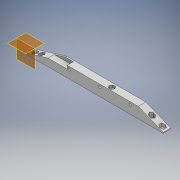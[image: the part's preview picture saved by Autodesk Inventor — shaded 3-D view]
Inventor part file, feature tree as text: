
AUTODESK INVENTOR PART (.ipt)
format: ipt  version: 2019 (Build 230136000, 136)  size: 250,368 bytes
history: native  units: mm
features: extrude x11, sketch x10, plane x7
ambient origin geometry x8: Origin, YZ Plane, XZ Plane, XY Plane, X Axis, Y Axis, Z Axis, Center Point
bodies: Solid1 (feature_tree)
feature tree (28):
  sketch  "Sketch1"  dims[d1=9.0mm d2=90.0deg]
  plane  "Work Plane2"
  sketch  "Sketch2"  dims[d6=3.2mm d7=3.2mm]
  plane  "Work Plane1"
  extrude  "klocek"  TaperAngle=90.0deg  [1 undecoded]
  plane  "Work Plane3"
  extrude  "prowadzenie osi"  Depth=3.2mm
  plane  "Work Plane4"
  sketch  "Sketch7"  dims[d15=3.2mm d17=3.2mm]
  sketch  "Sketch8"  dims[d18=36.5mm d26=3.2mm]
  extrude  "przedni skos"  Depth=3.2mm
  extrude  "tylni skos"  Depth=3.2mm
  plane  "Work Plane7"
  sketch  "Sketch5"  dims[d9=60.5mm d13=3.2mm]
  extrude  "hex insert middle"  Depth=3.2mm
  plane  "Work Plane6"
  sketch  "Sketch9"  dims[d27=48.0mm d28=3.2mm]
  extrude  "hex insert rear 1"  Depth=3.2mm
  plane  "Work Plane5"
  extrude  "hex insert rear 2"  Depth=5.0mm
  extrude  "hex insert front 1"  TaperAngle=0.0deg  [1 undecoded]
  extrude  "hex insert front 2"  Depth=8.0mm
  extrude  "ciecie przod"  Depth=5.9mm
  extrude  "sensor linii"  Depth=5.9mm
  sketch  "Sketch10"  dims[d32=15.0mm d33=5.0mm]
  sketch  "Sketch16"  dims[d38=11.0mm d39=0.0mm]
  sketch  "Sketch17"  dims[d61=3.2mm d62=8.0mm]
  sketch  "Sketch18"  dims[d63=12.5mm d64=52.0mm d65=36.5mm d67=13.0mm d68=0.0mm d70=7.5mm d71=0.0mm d77=5.0mm d78=0.0mm d80=12.0mm d81=30.0mm d82=3.0mm d83=0.0mm d84=8.5mm d85=0.0mm d86=12.0mm d87=40.0mm d88=7.0mm d89=0.0mm d91=9.0mm d92=0.0mm d93=5.9mm d94=9.0mm d95=0.0mm d96=10.0mm d97=0.0mm d98=5.9mm d99=5.9mm d102=4.0mm d103=25.0mm d104=2.5mm d105=7.3mm d106=0.0mm d108=4.0mm d109=4.0mm d111=4.0mm d112=4.0mm d113=4.0mm d114=10.0mm d115=73.0mm d118=5.9mm d122=2.0mm d123=5.9mm]
note: 2 required parameter values undecoded (feature->parameter linkage not recoverable at this tier; creation-order binding heuristic only, values carry confidence <= 0.55)
